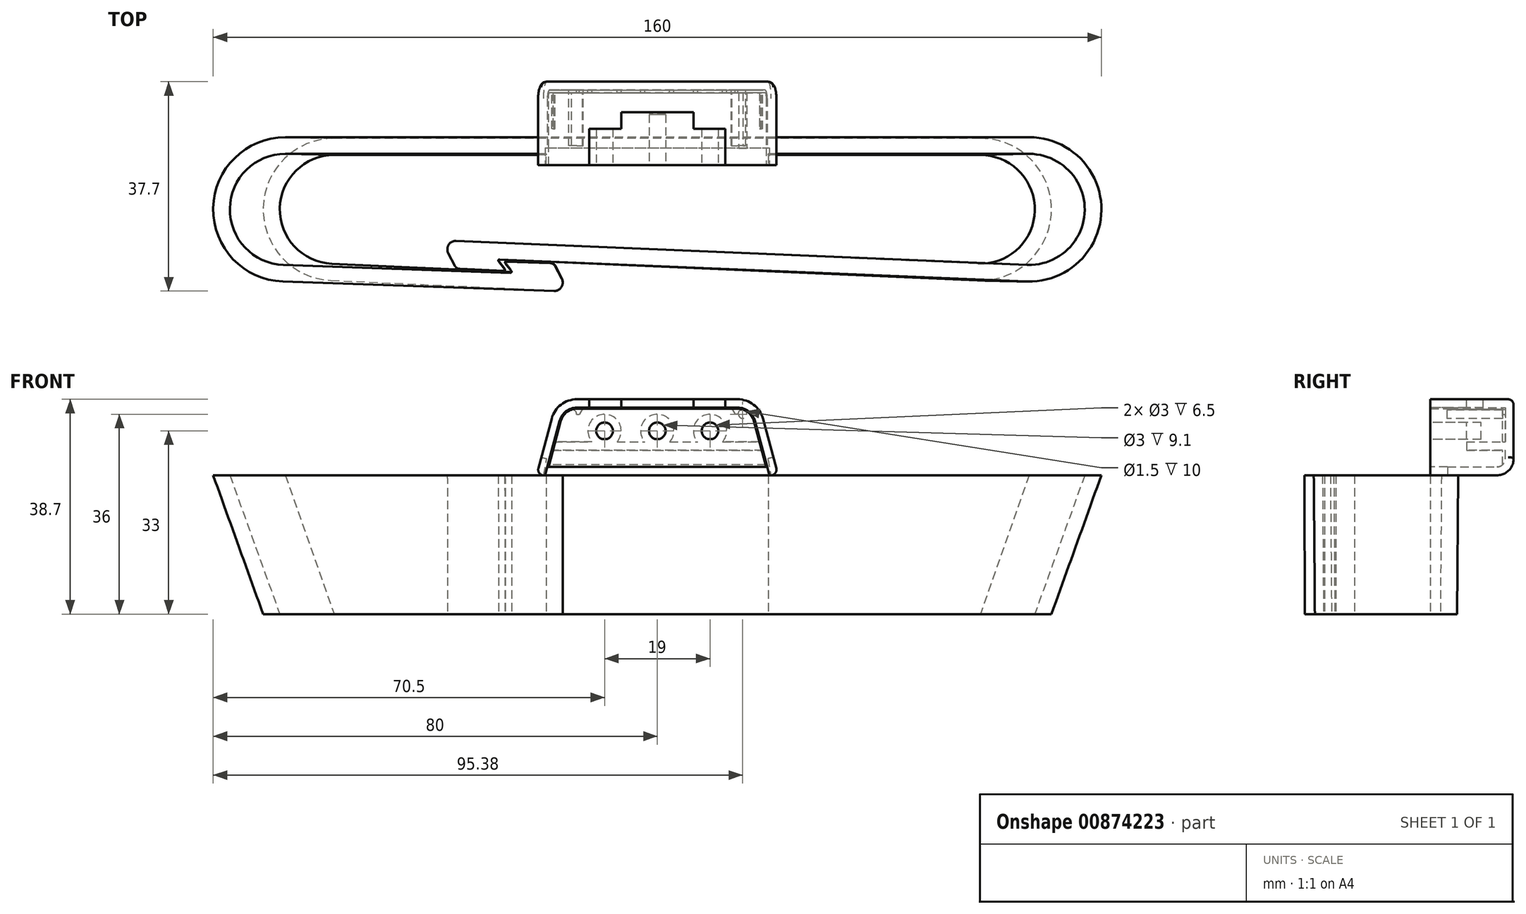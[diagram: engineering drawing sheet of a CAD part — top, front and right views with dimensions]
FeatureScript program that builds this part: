
annotation { "Feature Type Name" : "Feature", "Feature Type Description" : "" }
export const myFeature = defineFeature(function(context is Context, id is Id, definition is map)
    precondition{}
    {
        {
            var Q0;
            Q0=qCreatedBy(makeId("Top.planeOp"),FACE);
            var sketch = newSketch(context, id + "F0", { "sketchPlane" : qUnion([Q0])});
            skPoint(sketch, "E0.middle", {"position": v(0, 0) * mm});
            skArc(sketch, "E1", {"start": v(66.46, -12.99) * mm, "mid": v(80, -0.27) * mm, "end": v(67, 13) * mm});
            skLineSegment(sketch, "E2", {"start": v(67, 13) * mm, "end": v(-67, 13) * mm});
            skArc(sketch, "E3", {"start": v(-67, 13) * mm, "mid": v(-80, 0.23) * mm, "end": v(-67.45, -13) * mm});
            skLineSegment(sketch, "E4", {"start": v(66.46, -12.99) * mm, "end": v(-28.42, -9.01) * mm});
            skLineSegment(sketch, "E5", {"start": v(0, 13) * mm, "end": v(0, -10.2) * mm, "construction": true});
            skLineSegment(sketch, "E6", {"start": v(-16, 0) * mm, "end": v(-16, -14.79) * mm, "construction": true});
            skLineSegment(sketch, "E7", {"start": v(-67.45, -13) * mm, "end": v(-18.6, -14.7) * mm});
            skLineSegment(sketch, "E8", {"start": v(-67, 0) * mm, "end": v(-16, 0) * mm, "construction": true});
            skLineSegment(sketch, "E9.0", {"start": v(66.58, -10) * mm, "end": v(-36.26, -5.68) * mm});
            skLineSegment(sketch, "E9.1", {"start": v(-67.35, -10) * mm, "end": v(-26.46, -11.42) * mm});
            skArc(sketch, "E9.2", {"start": v(-67, 10) * mm, "mid": v(-77, 0.17) * mm, "end": v(-67.35, -10) * mm});
            skLineSegment(sketch, "E9.3", {"start": v(67, 10) * mm, "end": v(-67, 10) * mm});
            skArc(sketch, "E9.4", {"start": v(66.58, -10) * mm, "mid": v(77, -0.2) * mm, "end": v(67, 10) * mm});
            skLineSegment(sketch, "E10", {"start": v(-27.2, -9.4) * mm, "end": v(-19.29, -9.67) * mm});
            skLineSegment(sketch, "E11", {"start": v(-18.44, -10.2) * mm, "end": v(-17.22, -12.5) * mm});
            skPoint(sketch, "E12.visualSharp", {"position": v(-16, -14.79) * mm});
            skArc(sketch, "E12.filletArc", {"start": v(-18.6, -14.7) * mm, "mid": v(-17.27, -14) * mm, "end": v(-17.22, -12.5) * mm});
            skPoint(sketch, "E13.visualSharp", {"position": v(-18.71, -9.7) * mm});
            skArc(sketch, "E13.filletArc", {"start": v(-18.44, -10.2) * mm, "mid": v(-18.8, -9.82) * mm, "end": v(-19.29, -9.67) * mm});
            skPoint(sketch, "E14.visualSharp", {"position": v(-27.2, -9.4) * mm});
            skArc(sketch, "E14.filletArc", {"start": v(-27.2, -9.4) * mm, "mid": v(-27.4, -9.5) * mm, "end": v(-27.37, -9.72) * mm});
            skLineSegment(sketch, "E15", {"start": v(0, 0) * mm, "end": v(67, 0) * mm, "construction": true});
            skLineSegment(sketch, "E16", {"start": v(-28.59, -9.33) * mm, "end": v(-27.52, -10.72) * mm});
            skLineSegment(sketch, "E17", {"start": v(-27.69, -11.04) * mm, "end": v(-35.6, -10.71) * mm});
            skLineSegment(sketch, "E18", {"start": v(-36.45, -10.18) * mm, "end": v(-37.65, -7.87) * mm});
            skPoint(sketch, "E19.visualSharp", {"position": v(-36.18, -10.69) * mm});
            skArc(sketch, "E19.filletArc", {"start": v(-36.45, -10.18) * mm, "mid": v(-36.1, -10.56) * mm, "end": v(-35.6, -10.71) * mm});
            skPoint(sketch, "E20.visualSharp", {"position": v(-38.85, -5.57) * mm});
            skArc(sketch, "E20.filletArc", {"start": v(-36.26, -5.68) * mm, "mid": v(-37.59, -6.38) * mm, "end": v(-37.65, -7.87) * mm});
            skArc(sketch, "E21.filletArc", {"start": v(-27.69, -11.04) * mm, "mid": v(-27.5, -10.94) * mm, "end": v(-27.52, -10.72) * mm});
            skPoint(sketch, "E22.visualSharp", {"position": v(-28.85, -9) * mm});
            skArc(sketch, "E22.filletArc", {"start": v(-28.42, -9.01) * mm, "mid": v(-28.6, -9.12) * mm, "end": v(-28.59, -9.33) * mm});
            skLineSegment(sketch, "E23", {"start": v(-16, 0) * mm, "end": v(0, 0) * mm, "construction": true});
            skArc(sketch, "E24", {"start": v(-26.46, -11.42) * mm, "mid": v(-26.27, -11.31) * mm, "end": v(-26.3, -11.1) * mm});
            skLineSegment(sketch, "E25", {"start": v(-27.37, -9.72) * mm, "end": v(-26.3, -11.1) * mm});
            skLineSegment(sketch, "E26", {"start": v(-27.37, -9.47) * mm, "end": v(-27.37, -10.97) * mm, "construction": true});
            skLineSegment(sketch, "E27", {"start": v(-27.52, -10.72) * mm, "end": v(-27.52, -9.22) * mm, "construction": true});
            skSolve(sketch);
        }
        {
            var Q0;
            Q0=qCreatedBy(makeId("Top.planeOp"),FACE);
            cPlane(context, id + "F1", {"entities" : qUnion([Q0]), "cplaneType" : CPlaneType.OFFSET, "offset" : 25 * mm, "oppositeDirection" : true, "width" : 150 * mm, "height" : 150 * mm});
        }
        {
            var Q0;
            Q0=qCreatedBy(id+"F1.planeOp",FACE);
            var sketch = newSketch(context, id + "F2", { "sketchPlane" : qUnion([Q0])});
            skPoint(sketch, "E28.middle", {"position": v(0, 0) * mm});
            skArc(sketch, "E29", {"start": v(57.64, -12.79) * mm, "mid": v(71, -0.28) * mm, "end": v(58.2, 12.8) * mm});
            skLineSegment(sketch, "E30", {"start": v(58.2, 12.8) * mm, "end": v(-58.2, 12.8) * mm});
            skArc(sketch, "E31", {"start": v(-58.2, 12.8) * mm, "mid": v(-71, 0.3) * mm, "end": v(-58.78, -12.79) * mm});
            skLineSegment(sketch, "E32", {"start": v(57.64, -12.79) * mm, "end": v(-28.37, -9.03) * mm});
            skLineSegment(sketch, "E33", {"start": v(0, 12.8) * mm, "end": v(0, -10.27) * mm, "construction": true});
            skLineSegment(sketch, "E34", {"start": v(-16, 0) * mm, "end": v(-16, -14.73) * mm, "construction": true});
            skLineSegment(sketch, "E35", {"start": v(-58.78, -12.79) * mm, "end": v(-18.6, -14.61) * mm});
            skLineSegment(sketch, "E36", {"start": v(-58.2, 0) * mm, "end": v(-16, 0) * mm, "construction": true});
            skLineSegment(sketch, "E37.0", {"start": v(57.77, -9.8) * mm, "end": v(-36.2, -5.69) * mm});
            skLineSegment(sketch, "E37.1", {"start": v(-58.64, -9.79) * mm, "end": v(-26.42, -11.25) * mm});
            skArc(sketch, "E37.2", {"start": v(-58.2, 9.8) * mm, "mid": v(-68, 0.22) * mm, "end": v(-58.64, -9.79) * mm});
            skLineSegment(sketch, "E37.3", {"start": v(58.2, 9.8) * mm, "end": v(-58.2, 9.8) * mm});
            skArc(sketch, "E37.4", {"start": v(57.77, -9.8) * mm, "mid": v(68, -0.21) * mm, "end": v(58.2, 9.8) * mm});
            skLineSegment(sketch, "E38", {"start": v(-27.15, -9.22) * mm, "end": v(-19.23, -9.58) * mm});
            skLineSegment(sketch, "E39", {"start": v(-18.4, -10.12) * mm, "end": v(-17.2, -12.42) * mm});
            skPoint(sketch, "E40.visualSharp", {"position": v(-16, -14.73) * mm});
            skArc(sketch, "E40.filletArc", {"start": v(-18.6, -14.61) * mm, "mid": v(-17.26, -13.92) * mm, "end": v(-17.2, -12.42) * mm});
            skPoint(sketch, "E41.visualSharp", {"position": v(-18.66, -9.6) * mm});
            skArc(sketch, "E41.filletArc", {"start": v(-18.4, -10.12) * mm, "mid": v(-18.74, -9.73) * mm, "end": v(-19.23, -9.58) * mm});
            skPoint(sketch, "E42.visualSharp", {"position": v(-27.15, -9.22) * mm});
            skArc(sketch, "E42.filletArc", {"start": v(-27.15, -9.22) * mm, "mid": v(-27.33, -9.33) * mm, "end": v(-27.32, -9.54) * mm});
            skLineSegment(sketch, "E43", {"start": v(0, 0) * mm, "end": v(58.2, 0) * mm, "construction": true});
            skLineSegment(sketch, "E44", {"start": v(-28.53, -9.35) * mm, "end": v(-27.47, -10.74) * mm});
            skLineSegment(sketch, "E45", {"start": v(-27.63, -11.07) * mm, "end": v(-35.55, -10.72) * mm});
            skLineSegment(sketch, "E46", {"start": v(-36.4, -10.18) * mm, "end": v(-37.6, -7.88) * mm});
            skPoint(sketch, "E47.visualSharp", {"position": v(-36.13, -10.7) * mm});
            skArc(sketch, "E47.filletArc", {"start": v(-36.4, -10.18) * mm, "mid": v(-36.04, -10.57) * mm, "end": v(-35.55, -10.72) * mm});
            skPoint(sketch, "E48.visualSharp", {"position": v(-38.8, -5.57) * mm});
            skArc(sketch, "E48.filletArc", {"start": v(-36.2, -5.69) * mm, "mid": v(-37.53, -6.38) * mm, "end": v(-37.6, -7.88) * mm});
            skArc(sketch, "E49.filletArc", {"start": v(-27.63, -11.07) * mm, "mid": v(-27.45, -10.96) * mm, "end": v(-27.47, -10.74) * mm});
            skPoint(sketch, "E50.visualSharp", {"position": v(-28.8, -9.01) * mm});
            skArc(sketch, "E50.filletArc", {"start": v(-28.37, -9.03) * mm, "mid": v(-28.55, -9.14) * mm, "end": v(-28.53, -9.35) * mm});
            skLineSegment(sketch, "E51", {"start": v(-16, 0) * mm, "end": v(0, 0) * mm, "construction": true});
            skArc(sketch, "E52", {"start": v(-26.42, -11.25) * mm, "mid": v(-26.23, -11.15) * mm, "end": v(-26.25, -10.93) * mm});
            skLineSegment(sketch, "E53", {"start": v(-27.32, -9.54) * mm, "end": v(-26.25, -10.93) * mm});
            skLineSegment(sketch, "E54", {"start": v(-27.32, -9.3) * mm, "end": v(-27.32, -10.8) * mm, "construction": true});
            skLineSegment(sketch, "E55", {"start": v(-27.47, -10.74) * mm, "end": v(-27.47, -9.24) * mm, "construction": true});
            skSolve(sketch);
        }
        {
            var Q0;
            Q0=qSketchRegion(id+"F0",true);
            var Q1;
            Q1=qSketchRegion(id+"F2",true);
            loft(context, id + "F3", {"sheetProfilesArray" : [{ "sheetProfileEntities" : qUnion([Q0]) }, { "sheetProfileEntities" : qUnion([Q1]) }]});
        }
        {
            var Q0;
            Q0=qCreatedBy(makeId("Top.planeOp"),FACE);
            var sketch = newSketch(context, id + "F4", { "sketchPlane" : qUnion([Q0])});
            skLineSegment(sketch, "E56", {"start": v(20, 11) * mm, "end": v(20, 8) * mm});
            skLineSegment(sketch, "E57", {"start": v(-20, 8) * mm, "end": v(-20, 11) * mm});
            skLineSegment(sketch, "E58", {"start": v(0, 8) * mm, "end": v(0, 10) * mm, "construction": true});
            skPoint(sketch, "E58.endSnap0", {"position": v(0, 10) * mm});
            skLineSegment(sketch, "E59", {"start": v(-20, 8) * mm, "end": v(20, 8) * mm});
            skLineSegment(sketch, "E60", {"start": v(-20, 11) * mm, "end": v(20, 11) * mm});
            skSolve(sketch);
        }
        {
            var Q0;
            Q0=qSketchRegion(id+"F4",true);
            extrude(context, id + "F5", {"entities" : qUnion([Q0]), "operationType" : NewBodyOperationType.ADD, "depth" : 12 * mm, "offsetDistance" : 25 * mm, "hasSecondDirection" : true, "secondDirectionOppositeDirection" : true, "secondDirectionDepth" : 25 * mm});
        }
        {
            var Q0;
            Q0=makeQuery(id+"F5.opExtrude","SWEPT_FACE",FACE,{"disambiguationData":[OSD([sQuery(id+"F4.wireOp",EDGE,"E59")])]});
            var sketch = newSketch(context, id + "F6", { "sketchPlane" : qUnion([Q0])});
            skLineSegment(sketch, "E61", {"start": v(0, 12) * mm, "end": v(0, 8) * mm, "construction": true});
            skCircle(sketch, "E62", {"center": v(0, 8) * mm, "radius": 1.5 * mm});
            skCircle(sketch, "E63", {"center": v(9.5, 8) * mm, "radius": 1.5 * mm});
            skCircle(sketch, "E64", {"center": v(-9.5, 8) * mm, "radius": 1.5 * mm});
            skSolve(sketch);
        }
        {
            var Q0;
            Q0=qSketchRegion(id+"F6",true);
            extrude(context, id + "F7", {"entities" : qUnion([Q0]), "operationType" : NewBodyOperationType.REMOVE, "endBound" : BoundingType.THROUGH_ALL, "oppositeDirection" : true, "depth" : 25 * mm, "offsetDistance" : 25 * mm});
        }
        {
            var Q0;
            Q0=makeQuery(id+"F5.opExtrude","CAP_EDGE",EDGE,{"disambiguationData":[OSD([sQuery(id+"F4.wireOp",EDGE,"E57")])],"isStart":false});
            var Q1;
            Q1=makeQuery(id+"F5.opExtrude","CAP_EDGE",EDGE,{"disambiguationData":[OSD([sQuery(id+"F4.wireOp",EDGE,"E56")])],"isStart":false});
            chamfer(context, id + "F8", {"entities" : qUnion([Q0, Q1]), "chamferType" : ChamferType.OFFSET_ANGLE, "width" : 12 * mm, "oppositeDirection" : false, "angle" : 15 * degree, "tangentPropagation" : true});
        }
        {
            var Q0;
            {var subQ0=sQuery(id+"F4.wireOp",EDGE,"E57");Q0=makeQuery(id+"F8.opChamfer","BLEND_EDGE",EDGE,{"blendedFrom":[makeQuery(id+"F5.opExtrude","CAP_EDGE",EDGE,{"disambiguationData":[OSD([subQ0])],"isStart":false}),makeQuery(id+"F5.opExtrude","CAP_FACE",FACE,{"disambiguationData":[OSD([sQuery(id+"F4.wireOp",EDGE,"E56"),sQuery(id+"F4.wireOp",EDGE,"wCvbTNE0-mzVd-2HxN-2LCz-JJ2DgGp3YGLQ"),subQ0,sQuery(id+"F4.wireOp",EDGE,"oFSy1M9t-5aWS-44CZ-ftMe-uW2eaNrki7Xb")])],"isStart":false})],"blendedInto":[makeQuery(id+"F5.opExtrude","CAP_FACE",FACE,{"disambiguationData":[OSD([sQuery(id+"F4.wireOp",EDGE,"E56"),sQuery(id+"F4.wireOp",EDGE,"wCvbTNE0-mzVd-2HxN-2LCz-JJ2DgGp3YGLQ"),subQ0,sQuery(id+"F4.wireOp",EDGE,"oFSy1M9t-5aWS-44CZ-ftMe-uW2eaNrki7Xb")])],"isStart":false})]});}
            var Q1;
            {var subQ0=sQuery(id+"F4.wireOp",EDGE,"E56");Q1=makeQuery(id+"F8.opChamfer","BLEND_EDGE",EDGE,{"blendedFrom":[makeQuery(id+"F5.opExtrude","CAP_EDGE",EDGE,{"disambiguationData":[OSD([subQ0])],"isStart":false}),makeQuery(id+"F5.opExtrude","CAP_FACE",FACE,{"disambiguationData":[OSD([subQ0,sQuery(id+"F4.wireOp",EDGE,"wCvbTNE0-mzVd-2HxN-2LCz-JJ2DgGp3YGLQ"),sQuery(id+"F4.wireOp",EDGE,"E57"),sQuery(id+"F4.wireOp",EDGE,"oFSy1M9t-5aWS-44CZ-ftMe-uW2eaNrki7Xb")])],"isStart":false})],"blendedInto":[makeQuery(id+"F5.opExtrude","CAP_FACE",FACE,{"disambiguationData":[OSD([subQ0,sQuery(id+"F4.wireOp",EDGE,"wCvbTNE0-mzVd-2HxN-2LCz-JJ2DgGp3YGLQ"),sQuery(id+"F4.wireOp",EDGE,"E57"),sQuery(id+"F4.wireOp",EDGE,"oFSy1M9t-5aWS-44CZ-ftMe-uW2eaNrki7Xb")])],"isStart":false})]});}
            fillet(context, id + "F9", {"entities" : qUnion([Q0, Q1]), "radius" : 3 * mm, "tangentPropagation" : true, "allowEdgeOverflow" : false});
        }
        {
            var Q0;
            Q0=makeQuery(id+"F5.opExtrude","SWEPT_FACE",FACE,{"disambiguationData":[OSD([sQuery(id+"F4.wireOp",EDGE,"E59")])]});
            cPlane(context, id + "F10", {"entities" : qUnion([Q0]), "cplaneType" : CPlaneType.OFFSET, "offset" : 0 * mm, "oppositeDirection" : true, "width" : 150 * mm, "height" : 150 * mm});
        }
        {
            var Q0;
            Q0=qCreatedBy(id+"F10.planeOp",FACE);
            var sketch = newSketch(context, id + "F11", { "sketchPlane" : qUnion([Q0])});
            skLineSegment(sketch, "E65.0", {"start": v(-19.02, 10.22) * mm, "end": v(-21.76, 0) * mm});
            skLineSegment(sketch, "E65.1", {"start": v(21.76, 0) * mm, "end": v(19.02, 10.22) * mm});
            skArc(sketch, "E65.2", {"start": v(19.02, 10.22) * mm, "mid": v(17.34, 12.73) * mm, "end": v(14.48, 13.7) * mm});
            skLineSegment(sketch, "E65.3", {"start": v(-14.48, 13.7) * mm, "end": v(14.48, 13.7) * mm});
            skArc(sketch, "E65.4", {"start": v(-14.48, 13.7) * mm, "mid": v(-17.34, 12.73) * mm, "end": v(-19.02, 10.22) * mm});
            skLineSegment(sketch, "E66", {"start": v(-21.76, 0) * mm, "end": v(21.76, 0) * mm});
            skSolve(sketch);
        }
        {
            var Q0;
            Q0=qSketchRegion(id+"F11",true);
            extrude(context, id + "F12", {"entities" : qUnion([Q0]), "oppositeDirection" : true, "depth" : 15 * mm, "offsetDistance" : 25 * mm});
        }
        {
            var Q0;
            Q0=makeQuery(id+"F12.opExtrude","CAP_EDGE",EDGE,{"disambiguationData":[OSD([sQuery(id+"F11.wireOp",EDGE,"E66")])],"isStart":false});
            fillet(context, id + "F13", {"entities" : qUnion([Q0]), "radius" : 3 * mm, "tangentPropagation" : true, "allowEdgeOverflow" : false});
        }
        {
            var Q0;
            Q0=makeQuery(id+"F12.opExtrude","CAP_FACE",FACE,{"disambiguationData":[OSD([sQuery(id+"F11.wireOp",EDGE,"E65.0"),sQuery(id+"F11.wireOp",EDGE,"E65.1"),sQuery(id+"F11.wireOp",EDGE,"E65.2"),sQuery(id+"F11.wireOp",EDGE,"E65.3"),sQuery(id+"F11.wireOp",EDGE,"E65.4"),sQuery(id+"F11.wireOp",EDGE,"E66")])],"isStart":true});
            shell(context, id + "F14", {"entities" : qUnion([Q0]), "thickness" : 1.5 * mm});
        }
        {
            var Q0;
            Q0=makeQuery(id+"F12.opExtrude","CAP_FACE",FACE,{"disambiguationData":[OSD([sQuery(id+"F11.wireOp",EDGE,"E65.0"),sQuery(id+"F11.wireOp",EDGE,"E65.1"),sQuery(id+"F11.wireOp",EDGE,"E65.2"),sQuery(id+"F11.wireOp",EDGE,"E65.3"),sQuery(id+"F11.wireOp",EDGE,"E65.4"),sQuery(id+"F11.wireOp",EDGE,"E66")])],"isStart":true});
            var sketch = newSketch(context, id + "F15", { "sketchPlane" : qUnion([Q0])});
            skLineSegment(sketch, "E67", {"start": v(-19.8, 1.5) * mm, "end": v(19.8, 1.5) * mm});
            skLineSegment(sketch, "E68", {"start": v(19.8, 1.5) * mm, "end": v(20.2, 0) * mm});
            skLineSegment(sketch, "E69", {"start": v(20.2, 0) * mm, "end": v(-20.2, 0) * mm});
            skLineSegment(sketch, "E70", {"start": v(-20.2, 0) * mm, "end": v(-19.8, 1.5) * mm});
            skPoint(sketch, "E71", {"position": v(0, 0) * mm});
            skSolve(sketch);
        }
        {
            var Q0;
            Q0=qSketchRegion(id+"F15",true);
            extrude(context, id + "F16", {"entities" : qUnion([Q0]), "operationType" : NewBodyOperationType.REMOVE, "oppositeDirection" : true, "depth" : 3.1 * mm, "offsetDistance" : 25 * mm});
        }
        {
            var Q0;
            Q0=makeQuery(id+"F12.opExtrude","SWEPT_EDGE",EDGE,{"disambiguationData":[OSD([sQuery(id+"F11.wireOp",EDGE,"E65.1"),sQuery(id+"F11.wireOp",EDGE,"E66")])]});
            fillet(context, id + "F17", {"entities" : qUnion([Q0]), "radius" : 1 * mm, "tangentPropagation" : true, "allowEdgeOverflow" : false});
        }
        {
            var Q0;
            Q0=makeQuery(id+"F14.opShell","OFFSET_FACE",FACE,{"disambiguationData":[OSD([sQuery(id+"F11.wireOp",EDGE,"E65.0"),sQuery(id+"F11.wireOp",EDGE,"E65.1"),sQuery(id+"F11.wireOp",EDGE,"E65.2"),sQuery(id+"F11.wireOp",EDGE,"E65.3"),sQuery(id+"F11.wireOp",EDGE,"E65.4"),sQuery(id+"F11.wireOp",EDGE,"E66")])]});
            var sketch = newSketch(context, id + "F18", { "sketchPlane" : qUnion([Q0])});
            skCircle(sketch, "E72", {"center": v(0, 8) * mm, "radius": 3 * mm});
            skCircle(sketch, "E73", {"center": v(9.5, 8) * mm, "radius": 3 * mm});
            skCircle(sketch, "E74", {"center": v(-9.5, 8) * mm, "radius": 3 * mm});
            skLineSegment(sketch, "E75", {"start": v(-18.6, 6) * mm, "end": v(18.6, 6) * mm});
            skLineSegment(sketch, "E76", {"start": v(18.6, 6) * mm, "end": v(19, 4.5) * mm});
            skLineSegment(sketch, "E77", {"start": v(19, 4.5) * mm, "end": v(-19, 4.5) * mm});
            skLineSegment(sketch, "E78", {"start": v(-19, 4.5) * mm, "end": v(-18.6, 6) * mm});
            skSolve(sketch);
        }
        {
            var Q0;
            Q0=makeQuery(id+"F18.imprint","IMPRINT",FACE,{"disambiguationData":[TD([[makeQuery(id+"F18.imprint","IMPRINT",EDGE,{"derivedFrom":sQuery(id+"F18.wireOp",EDGE,"E74")}),1.0]])]});
            var Q1;
            Q1=makeQuery(id+"F18.imprint","IMPRINT",FACE,{"disambiguationData":[TD([[makeQuery(id+"F18.imprint","IMPRINT",EDGE,{"derivedFrom":sQuery(id+"F18.wireOp",EDGE,"E73")}),1.0]])]});
            var Q2;
            {var subQ0=sQuery(id+"F18.wireOp",EDGE,"E76");Q2=makeQuery(id+"F18.imprint","IMPRINT",FACE,{"disambiguationData":[TD([[makeQuery(id+"F18.imprint","IMPRINT",EDGE,{"derivedFrom":subQ0}),1.0]])]});}
            var Q3;
            {var subQ0=sQuery(id+"F18.wireOp",EDGE,"E75");var subQ1=sQuery(id+"F18.wireOp",EDGE,"E72");var subQ2=makeQuery(id+"F18.imprint","INTERSECT",VERTEX,{"disambiguationData":[OD(0.0)],"derivedFrom":[subQ1,subQ0]});Q3=makeQuery(id+"F18.imprint","IMPRINT",FACE,{"disambiguationData":[TD([[makeQuery(id+"F18.imprint","IMPRINT",EDGE,{"disambiguationData":[TD([[subQ2,1.0]])],"derivedFrom":subQ1}),1.0]])]});}
            var Q4;
            {var subQ0=sQuery(id+"F18.wireOp",EDGE,"E75");var subQ1=sQuery(id+"F18.wireOp",EDGE,"E72");var subQ2=makeQuery(id+"F18.imprint","INTERSECT",VERTEX,{"disambiguationData":[OD(0.0)],"derivedFrom":[subQ1,subQ0]});Q4=makeQuery(id+"F18.imprint","IMPRINT",FACE,{"disambiguationData":[TD([[makeQuery(id+"F18.imprint","IMPRINT",EDGE,{"disambiguationData":[TD([[subQ2,-1.0]])],"derivedFrom":subQ1}),1.0]])]});}
            extrude(context, id + "F19", {"entities" : qUnion([Q0, Q1, Q2, Q3, Q4]), "operationType" : NewBodyOperationType.ADD, "depth" : 7 * mm, "offsetDistance" : 25 * mm});
        }
        {
            var Q0;
            Q0=makeQuery(id+"F12.opExtrude","SWEPT_FACE",FACE,{"disambiguationData":[OSD([sQuery(id+"F11.wireOp",EDGE,"E65.3")])]});
            var sketch = newSketch(context, id + "F20", { "sketchPlane" : qUnion([Q0])});
            skLineSegment(sketch, "E79", {"start": v(-12.25, 8) * mm, "end": v(-12.25, 14.5) * mm});
            skLineSegment(sketch, "E80", {"start": v(-12.25, 14.5) * mm, "end": v(-6.5, 14.5) * mm});
            skLineSegment(sketch, "E81", {"start": v(-6.5, 14.5) * mm, "end": v(-6.5, 17.5) * mm});
            skLineSegment(sketch, "E82", {"start": v(-6.5, 17.5) * mm, "end": v(6.5, 17.5) * mm});
            skLineSegment(sketch, "E83", {"start": v(6.5, 17.5) * mm, "end": v(6.5, 14.5) * mm});
            skLineSegment(sketch, "E84", {"start": v(6.5, 14.5) * mm, "end": v(12.25, 14.5) * mm});
            skLineSegment(sketch, "E85", {"start": v(12.25, 14.5) * mm, "end": v(12.25, 8) * mm});
            skLineSegment(sketch, "E86", {"start": v(12.25, 8) * mm, "end": v(-12.25, 8) * mm});
            skPoint(sketch, "E87", {"position": v(0, 8) * mm});
            skSolve(sketch);
        }
        {
            var Q0;
            Q0=qSketchRegion(id+"F20",true);
            extrude(context, id + "F21", {"entities" : qUnion([Q0]), "operationType" : NewBodyOperationType.REMOVE, "oppositeDirection" : true, "depth" : 1.5 * mm, "offsetDistance" : 25 * mm});
        }
        {
            var Q0;
            {var subQ0=sQuery(id+"F11.wireOp",EDGE,"E66");Q0=makeQuery(id+"F14.opShell","OFFSET_FACE",FACE,{"disambiguationData":[OSD([subQ0]),TDD([makeQuery(id+"F12.opExtrude","SWEPT_FACE",FACE,{"disambiguationData":[OSD([subQ0])]})])]});}
            var sketch = newSketch(context, id + "F22", { "sketchPlane" : qUnion([Q0])});
            skLineSegment(sketch, "E88.bottom", {"start": v(6.25, 11.1) * mm, "end": v(-6.25, 11.1) * mm});
            skLineSegment(sketch, "E88.top", {"start": v(6.25, 17.1) * mm, "end": v(-6.25, 17.1) * mm});
            skLineSegment(sketch, "E88.left", {"start": v(6.25, 11.1) * mm, "end": v(6.25, 17.1) * mm});
            skLineSegment(sketch, "E88.right", {"start": v(-6.25, 11.1) * mm, "end": v(-6.25, 17.1) * mm});
            skPoint(sketch, "E89", {"position": v(0, 11.1) * mm});
            skSolve(sketch);
        }
        {
            var Q0;
            Q0=makeQuery(id+"F22.imprint","IMPRINT",FACE,{"disambiguationData":[TD([[makeQuery(id+"F22.imprint","IMPRINT",EDGE,{"derivedFrom":sQuery(id+"F22.wireOp",EDGE,"E88.bottom")}),1.0]])]});
            extrude(context, id + "F23", {"entities" : qUnion([Q0]), "operationType" : NewBodyOperationType.REMOVE, "depth" : 25 * mm, "offsetDistance" : 25 * mm});
        }
        {
            var Q0;
            Q0=makeQuery(id+"F5.opExtrude","SWEPT_FACE",FACE,{"disambiguationData":[OSD([sQuery(id+"F4.wireOp",EDGE,"E60")])]});
            var sketch = newSketch(context, id + "F24", { "sketchPlane" : qUnion([Q0])});
            skLineSegment(sketch, "E90", {"start": v(14.48, 12) * mm, "end": v(14.48, 9.78) * mm, "construction": true});
            skLineSegment(sketch, "E91", {"start": v(14.48, 9.78) * mm, "end": v(17.38, 9.78) * mm, "construction": true});
            skLineSegment(sketch, "E92", {"start": v(0, 12) * mm, "end": v(0, 0) * mm, "construction": true});
            skCircle(sketch, "E93", {"center": v(15.38, 11) * mm, "radius": 0.75 * mm});
            skCircle(sketch, "E94.MirrorC", {"center": v(-15.38, 11) * mm, "radius": 0.75 * mm});
            skSolve(sketch);
        }
        {
            var Q0;
            Q0=makeQuery(id+"F24.imprint","IMPRINT",FACE,{"disambiguationData":[TD([[makeQuery(id+"F24.imprint","IMPRINT",EDGE,{"derivedFrom":sQuery(id+"F24.wireOp",EDGE,"E93")}),1.0]])]});
            var Q1;
            Q1=makeQuery(id+"F24.imprint","IMPRINT",FACE,{"disambiguationData":[TD([[makeQuery(id+"F24.imprint","IMPRINT",EDGE,{"derivedFrom":sQuery(id+"F24.wireOp",EDGE,"E94.MirrorC")}),-1.0]])]});
            extrude(context, id + "F25", {"entities" : qUnion([Q0, Q1]), "operationType" : NewBodyOperationType.ADD, "depth" : 10 * mm, "offsetDistance" : 25 * mm});
        }
        {
            var Q0;
            {var subQ3=sQuery(id+"F11.wireOp",EDGE,"E65.0");var subQ5=sQuery(id+"F11.wireOp",EDGE,"E65.1");var subQ6=sQuery(id+"F11.wireOp",EDGE,"E65.2");var subQ7=sQuery(id+"F11.wireOp",EDGE,"E65.3");var subQ8=sQuery(id+"F11.wireOp",EDGE,"E65.4");Q0=makeQuery(id+"F19.boolean.opBoolean","SPLIT",FACE,{"disambiguationData":[TD([makeQuery(id+"F14.opShell","OFFSET_FACE",FACE,{"disambiguationData":[OSD([subQ6])]})])],"derivedFrom":makeQuery(id+"F14.opShell","OFFSET_FACE",FACE,{"disambiguationData":[OSD([subQ3,subQ5,subQ6,subQ7,subQ8,sQuery(id+"F11.wireOp",EDGE,"E66")])]})});}
            var sketch = newSketch(context, id + "F26", { "sketchPlane" : qUnion([Q0])});
            skCircle(sketch, "E95", {"center": v(-15.38, 11) * mm, "radius": 0.85 * mm, "construction": true});
            skLineSegment(sketch, "E96", {"start": v(-15.38, 11.85) * mm, "end": v(-15.94, 11.85) * mm});
            skLineSegment(sketch, "E97", {"start": v(-14.53, 11) * mm, "end": v(-14.03, 11) * mm});
            skLineSegment(sketch, "E98", {"start": v(-13.34, 12.2) * mm, "end": v(-14.03, 11) * mm});
            skArc(sketch, "E99", {"start": v(-15.38, 11.85) * mm, "mid": v(-14.78, 11.6) * mm, "end": v(-14.53, 11) * mm});
            skLineSegment(sketch, "E100.MirrorCS", {"start": v(15.38, 11.85) * mm, "end": v(15.94, 11.85) * mm});
            skLineSegment(sketch, "E101.MirrorCS", {"start": v(14.53, 11) * mm, "end": v(14.03, 11) * mm});
            skLineSegment(sketch, "E102.MirrorCS", {"start": v(13.34, 12.2) * mm, "end": v(14.03, 11) * mm});
            skCircle(sketch, "E103.MirrorC", {"center": v(15.38, 11) * mm, "radius": 0.85 * mm, "construction": true});
            skArc(sketch, "E104", {"start": v(15.38, 11.85) * mm, "mid": v(14.78, 11.6) * mm, "end": v(14.53, 11) * mm});
            skSolve(sketch);
        }
        {
            var Q0;
            {var subQ5=sQuery(id+"F26.wireOp",EDGE,"E100.MirrorCS");Q0=makeQuery(id+"F26.imprint","IMPRINT",FACE,{"disambiguationData":[TD([[makeQuery(id+"F26.imprint","IMPRINT",EDGE,{"derivedFrom":subQ5}),1.0]])]});}
            var Q1;
            {var subQ6=sQuery(id+"F26.wireOp",EDGE,"E96");Q1=makeQuery(id+"F26.imprint","IMPRINT",FACE,{"disambiguationData":[TD([[makeQuery(id+"F26.imprint","IMPRINT",EDGE,{"derivedFrom":subQ6}),-1.0]])]});}
            var Q2;
            {var subQ0=sQuery(id+"F11.wireOp",EDGE,"E66");var subQ1=sQuery(id+"F11.wireOp",EDGE,"E65.4");var subQ2=sQuery(id+"F11.wireOp",EDGE,"E65.3");var subQ3=sQuery(id+"F11.wireOp",EDGE,"E65.0");Q2=makeQuery(id+"F21.boolean.opBoolean","SPLIT",FACE,{"disambiguationData":[TD([makeQuery(id+"F12.opExtrude","SWEPT_FACE",FACE,{"disambiguationData":[OSD([subQ3])]})])],"derivedFrom":makeQuery(id+"F12.opExtrude","CAP_FACE",FACE,{"disambiguationData":[OSD([subQ3,sQuery(id+"F11.wireOp",EDGE,"E65.1"),sQuery(id+"F11.wireOp",EDGE,"E65.2"),subQ2,subQ1,subQ0])],"isStart":true})});}
            extrude(context, id + "F27", {"entities" : qUnion([Q0, Q1]), "operationType" : NewBodyOperationType.ADD, "depth" : 10 * mm, "endBoundEntityFace" : qUnion([Q2]), "offsetDistance" : 25 * mm});
        }
    });
